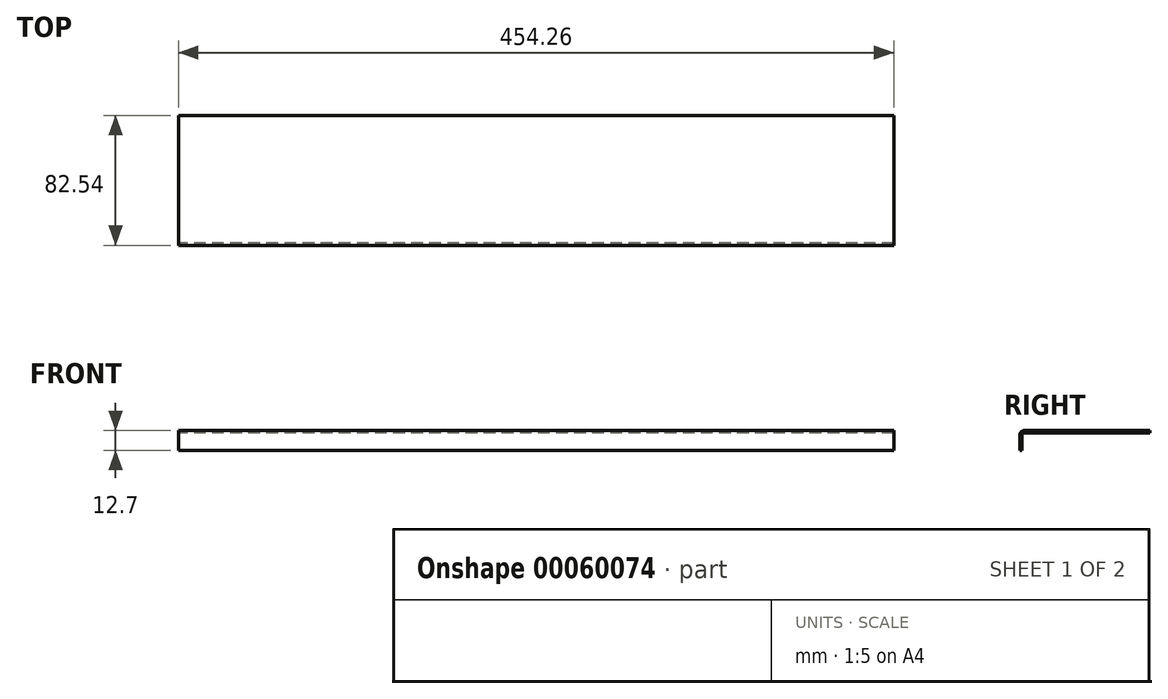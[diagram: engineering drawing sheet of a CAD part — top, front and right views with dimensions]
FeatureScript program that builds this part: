
annotation { "Feature Type Name" : "Feature", "Feature Type Description" : "" }
export const myFeature = defineFeature(function(context is Context, id is Id, definition is map)
    precondition{}
    {
        {
            var Q0;
            Q0=qCreatedBy(makeId("Top.planeOp"),FACE);
            var sketch = newSketch(context, id + "F0", { "sketchPlane" : qUnion([Q0])});
            skLineSegment(sketch, "E0.rect.bottom", {"start": v(241.3, -41.27) * mm, "end": v(-241.3, -41.28) * mm});
            skLineSegment(sketch, "E0.rect.top", {"start": v(241.3, 41.28) * mm, "end": v(-241.3, 41.27) * mm});
            skLineSegment(sketch, "E0.rect.left", {"start": v(241.3, -41.27) * mm, "end": v(241.3, 41.28) * mm});
            skLineSegment(sketch, "E0.rect.right", {"start": v(-241.3, -41.28) * mm, "end": v(-241.3, 41.27) * mm});
            skPoint(sketch, "E0.rect.middle", {"position": v(0, 0) * mm});
            skSolve(sketch);
        }
        {
            var Q0;
            Q0=qSketchRegion(id+"F0",true);
            extrude(context, id + "F1", {"entities" : qUnion([Q0]), "oppositeDirection" : true, "depth" : 12.7 * mm});
        }
        {
            var Q0;
            Q0=makeQuery(id+"F1.opExtrude","CAP_EDGE",EDGE,{"disambiguationData":[OSD([sQuery(id+"F0.wireOp",EDGE,"E0.rect.bottom")])],"isStart":true});
            fillet(context, id + "F2", {"entities" : qUnion([Q0]), "radius" : 3.17 * mm, "tangentPropagation" : true, "allowEdgeOverflow" : false});
        }
        {
            var Q0;
            Q0=makeQuery(id+"F1.opExtrude","CAP_FACE",FACE,{"disambiguationData":[OSD([sQuery(id+"F0.wireOp",EDGE,"E0.rect.bottom"),sQuery(id+"F0.wireOp",EDGE,"E0.rect.top"),sQuery(id+"F0.wireOp",EDGE,"E0.rect.left"),sQuery(id+"F0.wireOp",EDGE,"E0.rect.right")])],"isStart":false});
            var Q1;
            Q1=makeQuery(id+"F1.opExtrude","SWEPT_FACE",FACE,{"disambiguationData":[OSD([sQuery(id+"F0.wireOp",EDGE,"E0.rect.left")])]});
            var Q2;
            Q2=makeQuery(id+"F1.opExtrude","SWEPT_FACE",FACE,{"disambiguationData":[OSD([sQuery(id+"F0.wireOp",EDGE,"E0.rect.top")])]});
            var Q3;
            Q3=makeQuery(id+"F1.opExtrude","SWEPT_FACE",FACE,{"disambiguationData":[OSD([sQuery(id+"F0.wireOp",EDGE,"E0.rect.right")])]});
            shell(context, id + "F3", {"entities" : qUnion([Q0, Q1, Q2, Q3]), "thickness" : 1.52 * mm});
        }
        {
            var Q0;
            Q0=makeQuery(id+"F1.opExtrude","CAP_FACE",FACE,{"disambiguationData":[OSD([sQuery(id+"F0.wireOp",EDGE,"E0.rect.bottom"),sQuery(id+"F0.wireOp",EDGE,"E0.rect.top"),sQuery(id+"F0.wireOp",EDGE,"E0.rect.left"),sQuery(id+"F0.wireOp",EDGE,"E0.rect.right")])],"isStart":true});
            var sketch = newSketch(context, id + "F4", { "sketchPlane" : qUnion([Q0])});
            skLineSegment(sketch, "E1.bottom", {"start": v(-241.3, 41.27) * mm, "end": v(-227.13, 41.27) * mm});
            skLineSegment(sketch, "E1.top", {"start": v(-241.3, -41.28) * mm, "end": v(-227.13, -41.28) * mm});
            skLineSegment(sketch, "E1.left", {"start": v(-241.3, 41.27) * mm, "end": v(-241.3, -41.28) * mm});
            skLineSegment(sketch, "E1.right", {"start": v(-227.13, 41.27) * mm, "end": v(-227.13, -41.28) * mm});
            skLineSegment(sketch, "E2.bottom", {"start": v(241.3, 41.28) * mm, "end": v(227.13, 41.28) * mm});
            skLineSegment(sketch, "E2.top", {"start": v(241.3, -41.27) * mm, "end": v(227.13, -41.27) * mm});
            skLineSegment(sketch, "E2.left", {"start": v(241.3, 41.28) * mm, "end": v(241.3, -41.27) * mm});
            skLineSegment(sketch, "E2.right", {"start": v(227.13, 41.28) * mm, "end": v(227.13, -41.27) * mm});
            skSolve(sketch);
        }
        {
            var Q0;
            Q0=qSketchRegion(id+"F4",true);
            extrude(context, id + "F5", {"entities" : qUnion([Q0]), "operationType" : NewBodyOperationType.REMOVE, "oppositeDirection" : true, "depth" : 25.4 * mm});
        }
    });
